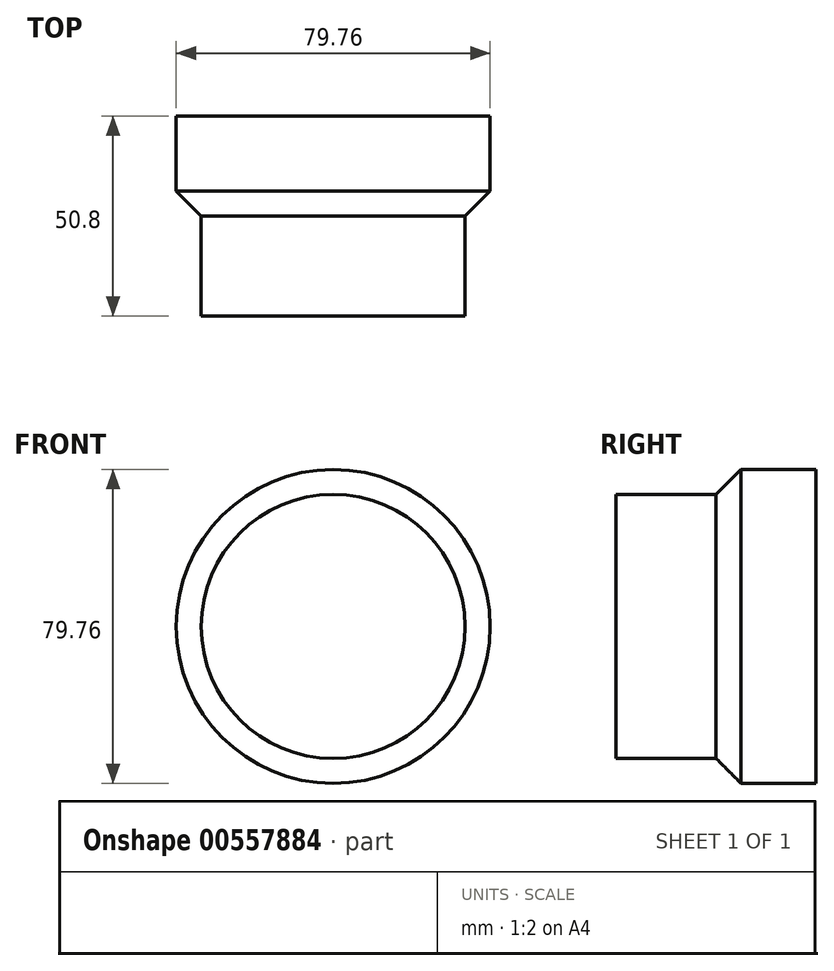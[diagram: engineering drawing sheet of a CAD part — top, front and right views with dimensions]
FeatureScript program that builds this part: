
annotation { "Feature Type Name" : "Feature", "Feature Type Description" : "" }
export const myFeature = defineFeature(function(context is Context, id is Id, definition is map)
    precondition{}
    {
        {
            var Q0;
            Q0=qCreatedBy(makeId("Front.planeOp"),FACE);
            var sketch = newSketch(context, id + "F0", { "sketchPlane" : qUnion([Q0])});
            skCircle(sketch, "E0", {"center": v(0, 0) * mm, "radius": 39.88 * mm});
            skSolve(sketch);
        }
        {
            var Q0;
            Q0=makeQuery(id+"F0.imprint","IMPRINT",FACE,{"disambiguationData":[TD([[makeQuery(id+"F0.imprint","IMPRINT",EDGE,{"derivedFrom":sQuery(id+"F0.wireOp",EDGE,"E0")}),1.0]])]});
            extrude(context, id + "F1", {"entities" : qUnion([Q0]), "depth" : 25.4 * mm, "offsetDistance" : 25.4 * mm});
        }
        {
            var Q0;
            Q0=makeQuery(id+"F1.opExtrude","CAP_EDGE",EDGE,{"disambiguationData":[OSD([sQuery(id+"F0.wireOp",EDGE,"E0")])],"isStart":false});
            chamfer(context, id + "F2", {"entities" : qUnion([Q0]), "width" : 6.35 * mm, "tangentPropagation" : true});
        }
        {
            var Q0;
            Q0=qCreatedBy(makeId("Front.planeOp"),FACE);
            var sketch = newSketch(context, id + "F3", { "sketchPlane" : qUnion([Q0])});
            skSolve(sketch);
        }
        {
            var Q0;
            Q0=makeQuery(id+"F1.opExtrude","CAP_FACE",FACE,{"disambiguationData":[OSD([sQuery(id+"F0.wireOp",EDGE,"E0")])],"isStart":false});
            extrude(context, id + "F4", {"entities" : qUnion([Q0]), "operationType" : NewBodyOperationType.ADD, "depth" : 25.4 * mm, "offsetDistance" : 25.4 * mm});
        }
    });
